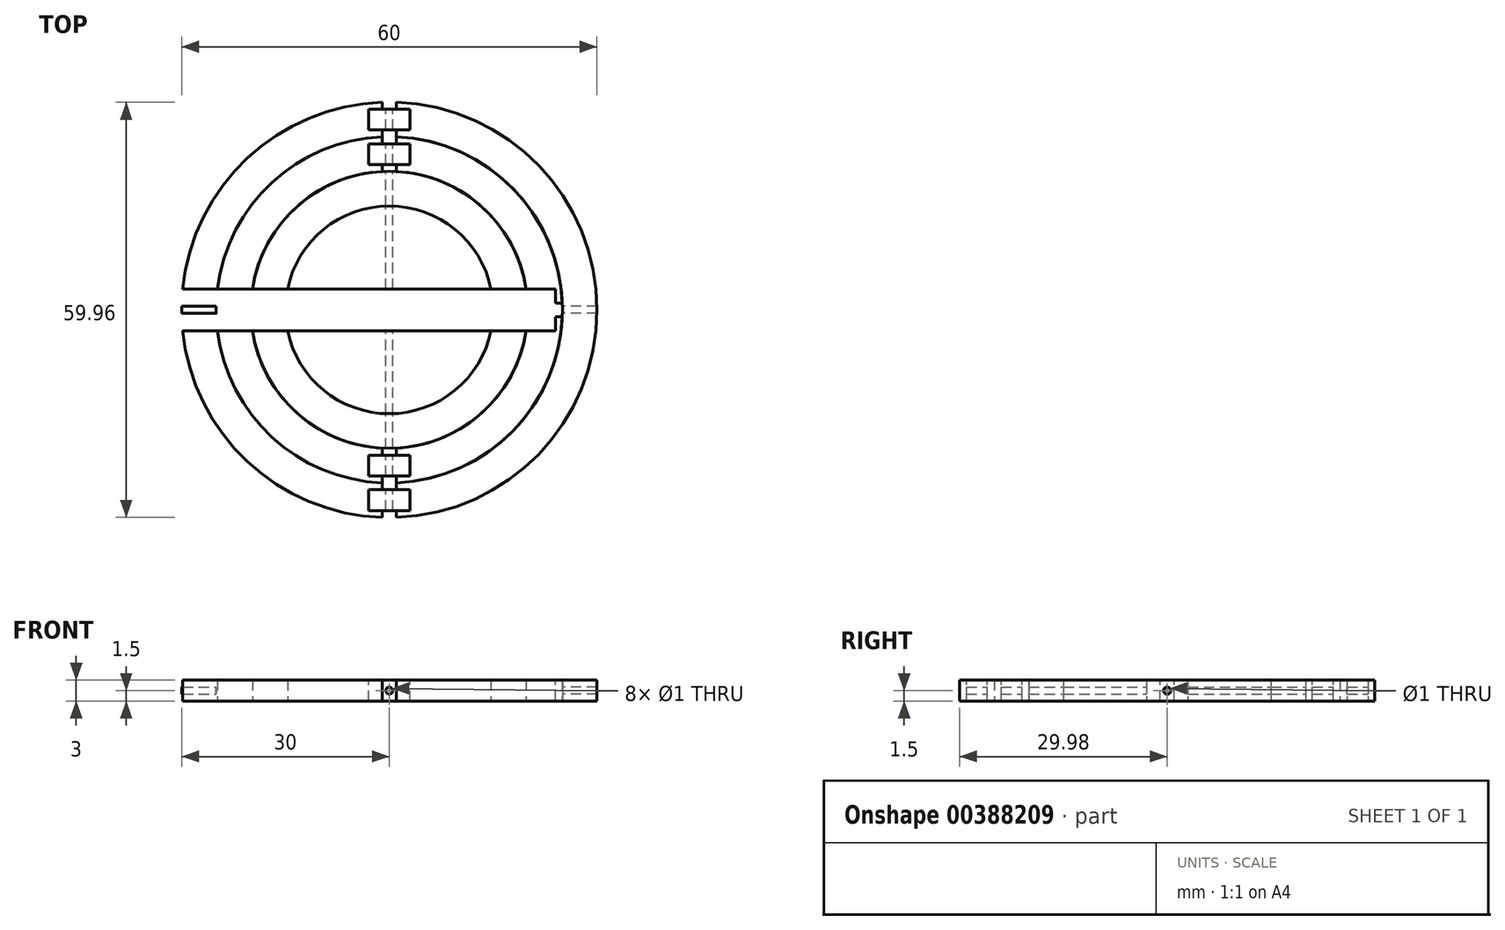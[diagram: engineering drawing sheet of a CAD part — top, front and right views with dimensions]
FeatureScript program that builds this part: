
annotation { "Feature Type Name" : "Feature", "Feature Type Description" : "" }
export const myFeature = defineFeature(function(context is Context, id is Id, definition is map)
    precondition{}
    {
        {
            assignVariable(context, id + "F0", {"name" : "WT", "anyValue" : 3});
        }
        {
            var Q0;
            Q0=qCreatedBy(makeId("Top.planeOp"),FACE);
            var sketch = newSketch(context, id + "F1", { "sketchPlane" : qUnion([Q0])});
            skCircle(sketch, "E0", {"center": v(0, 0) * mm, "radius": 30 * mm});
            skCircle(sketch, "E1", {"center": v(0, 0) * mm, "radius": 25 * mm});
            skCircle(sketch, "E2", {"center": v(0, 0) * mm, "radius": 20 * mm});
            skCircle(sketch, "E3", {"center": v(0, 0) * mm, "radius": 15 * mm});
            skLineSegment(sketch, "E4", {"start": v(-1, 29.98) * mm, "end": v(-1, 19.97) * mm});
            skLineSegment(sketch, "E5.MirrorCS", {"start": v(1, 29.98) * mm, "end": v(1, 19.97) * mm});
            skLineSegment(sketch, "E6.MirrorCS", {"start": v(-1, -29.98) * mm, "end": v(-1, -19.97) * mm});
            skLineSegment(sketch, "E7.MirrorCS", {"start": v(1, -29.98) * mm, "end": v(1, -19.97) * mm});
            skLineSegment(sketch, "E8", {"start": v(-14.97, 1) * mm, "end": v(-24.98, 1) * mm});
            skLineSegment(sketch, "E9.MirrorCS", {"start": v(-14.97, -1) * mm, "end": v(-24.98, -1) * mm});
            skLineSegment(sketch, "E10.MirrorCS", {"start": v(14.97, 1) * mm, "end": v(24.98, 1) * mm});
            skLineSegment(sketch, "E11.MirrorCS", {"start": v(14.97, -1) * mm, "end": v(24.98, -1) * mm});
            skSolve(sketch);
        }
        {
            var Q0;
            {var subQ5=sQuery(id+"F1.wireOp",EDGE,"E4");var subQ7=sQuery(id+"F1.wireOp",EDGE,"E0");var subQ9=makeQuery(id+"F1.imprint","INTERSECT",VERTEX,{"derivedFrom":[subQ7,subQ5]});Q0=makeQuery(id+"F1.imprint","IMPRINT",FACE,{"disambiguationData":[TD([[makeQuery(id+"F1.imprint","IMPRINT",EDGE,{"disambiguationData":[TD([[subQ9,-1.0]])],"derivedFrom":subQ7}),1.0]])]});}
            var Q1;
            {var subQ5=sQuery(id+"F1.wireOp",EDGE,"E5.MirrorCS");var subQ7=sQuery(id+"F1.wireOp",EDGE,"E0");var subQ8=makeQuery(id+"F1.imprint","INTERSECT",VERTEX,{"derivedFrom":[subQ7,subQ5]});Q1=makeQuery(id+"F1.imprint","IMPRINT",FACE,{"disambiguationData":[TD([[makeQuery(id+"F1.imprint","IMPRINT",EDGE,{"disambiguationData":[TD([[subQ8,1.0]])],"derivedFrom":subQ7}),1.0]])]});}
            extrude(context, id + "F2", {"entities" : qUnion([Q0, Q1]), "depth" : 1.5 * mm, "hasSecondDirection" : true, "secondDirectionOppositeDirection" : true, "secondDirectionDepth" : 1.5 * mm});
        }
        {
            var Q0;
            {var subQ0=sQuery(id+"F1.wireOp",EDGE,"E8");var subQ1=sQuery(id+"F1.wireOp",EDGE,"E1");var subQ2=makeQuery(id+"F1.imprint","INTERSECT",VERTEX,{"derivedFrom":[subQ1,subQ0]});Q0=makeQuery(id+"F1.imprint","IMPRINT",FACE,{"disambiguationData":[TD([[makeQuery(id+"F1.imprint","IMPRINT",EDGE,{"disambiguationData":[TD([[subQ2,1.0]])],"derivedFrom":subQ1}),1.0]])]});}
            var Q1;
            {var subQ0=sQuery(id+"F1.wireOp",EDGE,"E9.MirrorCS");var subQ1=sQuery(id+"F1.wireOp",EDGE,"E1");var subQ2=makeQuery(id+"F1.imprint","INTERSECT",VERTEX,{"derivedFrom":[subQ1,subQ0]});Q1=makeQuery(id+"F1.imprint","IMPRINT",FACE,{"disambiguationData":[TD([[makeQuery(id+"F1.imprint","IMPRINT",EDGE,{"disambiguationData":[TD([[subQ2,-1.0]])],"derivedFrom":subQ1}),1.0]])]});}
            var Q2;
            {var subQ0=sQuery(id+"F1.wireOp",EDGE,"E11.MirrorCS");var subQ1=sQuery(id+"F1.wireOp",EDGE,"E1");var subQ2=makeQuery(id+"F1.imprint","INTERSECT",VERTEX,{"derivedFrom":[subQ1,subQ0]});Q2=makeQuery(id+"F1.imprint","IMPRINT",FACE,{"disambiguationData":[TD([[makeQuery(id+"F1.imprint","IMPRINT",EDGE,{"disambiguationData":[TD([[subQ2,1.0]])],"derivedFrom":subQ1}),1.0]])]});}
            var Q3;
            {var subQ0=sQuery(id+"F1.wireOp",EDGE,"E10.MirrorCS");var subQ1=sQuery(id+"F1.wireOp",EDGE,"E1");var subQ2=makeQuery(id+"F1.imprint","INTERSECT",VERTEX,{"derivedFrom":[subQ1,subQ0]});Q3=makeQuery(id+"F1.imprint","IMPRINT",FACE,{"disambiguationData":[TD([[makeQuery(id+"F1.imprint","IMPRINT",EDGE,{"disambiguationData":[TD([[subQ2,-1.0]])],"derivedFrom":subQ1}),1.0]])]});}
            extrude(context, id + "F3", {"entities" : qUnion([Q0, Q1, Q2, Q3]), "depth" : 1.5 * mm, "hasSecondDirection" : true, "secondDirectionOppositeDirection" : true, "secondDirectionDepth" : 1.5 * mm});
        }
        {
            var Q0;
            {var subQ5=sQuery(id+"F1.wireOp",EDGE,"E2");var subQ9=makeQuery(id+"F1.imprint","INTERSECT",VERTEX,{"derivedFrom":[subQ5,sQuery(id+"F1.wireOp",EDGE,"E5.MirrorCS")]});Q0=makeQuery(id+"F1.imprint","IMPRINT",FACE,{"disambiguationData":[TD([[makeQuery(id+"F1.imprint","IMPRINT",EDGE,{"disambiguationData":[TD([[subQ9,1.0]])],"derivedFrom":subQ5}),1.0]])]});}
            var Q1;
            {var subQ0=sQuery(id+"F1.wireOp",EDGE,"E2");var subQ8=makeQuery(id+"F1.imprint","INTERSECT",VERTEX,{"derivedFrom":[subQ0,sQuery(id+"F1.wireOp",EDGE,"E6.MirrorCS")]});Q1=makeQuery(id+"F1.imprint","IMPRINT",FACE,{"disambiguationData":[TD([[makeQuery(id+"F1.imprint","IMPRINT",EDGE,{"disambiguationData":[TD([[subQ8,1.0]])],"derivedFrom":subQ0}),1.0]])]});}
            extrude(context, id + "F4", {"entities" : qUnion([Q0, Q1]), "depth" : 1.5 * mm, "hasSecondDirection" : true, "secondDirectionOppositeDirection" : true, "secondDirectionDepth" : 1.5 * mm});
        }
        {
            var Q0;
            {var subQ0=sQuery(id+"F1.wireOp",EDGE,"E3");var subQ1=makeQuery(id+"F1.imprint","INTERSECT",VERTEX,{"derivedFrom":[subQ0,sQuery(id+"F1.wireOp",EDGE,"E8")]});Q0=makeQuery(id+"F1.imprint","IMPRINT",FACE,{"disambiguationData":[TD([[makeQuery(id+"F1.imprint","IMPRINT",EDGE,{"disambiguationData":[TD([[subQ1,1.0]])],"derivedFrom":subQ0}),1.0]])]});}
            extrude(context, id + "F5", {"entities" : qUnion([Q0]), "depth" : (getVariable(context, 'WT')) / 2 * mm, "hasSecondDirection" : true, "secondDirectionOppositeDirection" : true, "secondDirectionDepth" : (getVariable(context, 'WT')) / 2 * mm});
        }
        {
            var Q0;
            Q0=makeQuery(id+"F2.opExtrude","CAP_FACE",FACE,{"disambiguationData":[OSD([sQuery(id+"F1.wireOp",EDGE,"E0"),sQuery(id+"F1.wireOp",EDGE,"E1"),sQuery(id+"F1.wireOp",EDGE,"E4"),sQuery(id+"F1.wireOp",EDGE,"E6.MirrorCS")])],"isStart":false});
            var sketch = newSketch(context, id + "F6", { "sketchPlane" : qUnion([Q0])});
            skLineSegment(sketch, "E12.0", {"start": v(-1, 29.98) * mm, "end": v(-1, 24.98) * mm, "construction": true});
            skLineSegment(sketch, "E13", {"start": v(-1, 27.48) * mm, "end": v(1, 27.48) * mm, "construction": true});
            skLineSegment(sketch, "E14.0", {"start": v(1, 29.98) * mm, "end": v(1, 24.98) * mm, "construction": true});
            skLineSegment(sketch, "E15.bottom", {"start": v(-3, 28.98) * mm, "end": v(3, 28.98) * mm});
            skLineSegment(sketch, "E15.top", {"start": v(-3, 25.98) * mm, "end": v(3, 25.98) * mm});
            skLineSegment(sketch, "E15.left", {"start": v(-3, 28.98) * mm, "end": v(-3, 25.98) * mm});
            skLineSegment(sketch, "E15.right", {"start": v(3, 28.98) * mm, "end": v(3, 25.98) * mm});
            skPoint(sketch, "E15.middle", {"position": v(0, 27.48) * mm});
            skLineSegment(sketch, "E16.0", {"start": v(-1, 24.98) * mm, "end": v(-1, 19.97) * mm, "construction": true});
            skLineSegment(sketch, "E17.0", {"start": v(1, 24.98) * mm, "end": v(1, 19.97) * mm, "construction": true});
            skLineSegment(sketch, "E18", {"start": v(-1, 22.48) * mm, "end": v(1, 22.48) * mm, "construction": true});
            skLineSegment(sketch, "E19.bottom", {"start": v(-3, 23.98) * mm, "end": v(3, 23.98) * mm});
            skLineSegment(sketch, "E19.top", {"start": v(-3, 20.98) * mm, "end": v(3, 20.98) * mm});
            skLineSegment(sketch, "E19.left", {"start": v(-3, 23.98) * mm, "end": v(-3, 20.98) * mm});
            skLineSegment(sketch, "E19.right", {"start": v(3, 23.98) * mm, "end": v(3, 20.98) * mm});
            skPoint(sketch, "E19.middle", {"position": v(0, 22.48) * mm});
            skLineSegment(sketch, "E20.0", {"start": v(-19.97, 1) * mm, "end": v(-24.98, 1) * mm});
            skLineSegment(sketch, "E21.0", {"start": v(-19.97, -1) * mm, "end": v(-24.98, -1) * mm});
            skLineSegment(sketch, "E22.0", {"start": v(-14.97, 1) * mm, "end": v(-19.97, 1) * mm});
            skLineSegment(sketch, "E23.0", {"start": v(-14.97, -1) * mm, "end": v(-19.97, -1) * mm});
            skLineSegment(sketch, "E24", {"start": v(-22.48, 1) * mm, "end": v(-22.48, -1) * mm, "construction": true});
            skLineSegment(sketch, "E25", {"start": v(-17.47, 1) * mm, "end": v(-17.47, -1) * mm, "construction": true});
            skLineSegment(sketch, "E26.bottom", {"start": v(-23.98, 3) * mm, "end": v(-20.98, 3) * mm});
            skLineSegment(sketch, "E26.top", {"start": v(-23.98, -3) * mm, "end": v(-20.98, -3) * mm});
            skLineSegment(sketch, "E26.left", {"start": v(-23.98, 3) * mm, "end": v(-23.98, -3) * mm});
            skLineSegment(sketch, "E26.right", {"start": v(-20.98, 3) * mm, "end": v(-20.98, -3) * mm});
            skPoint(sketch, "E26.middle", {"position": v(-22.48, 0) * mm});
            skLineSegment(sketch, "E27.bottom", {"start": v(-18.97, 3) * mm, "end": v(-15.97, 3) * mm});
            skLineSegment(sketch, "E27.top", {"start": v(-18.97, -3) * mm, "end": v(-15.97, -3) * mm});
            skLineSegment(sketch, "E27.left", {"start": v(-18.97, 3) * mm, "end": v(-18.97, -3) * mm});
            skLineSegment(sketch, "E27.right", {"start": v(-15.97, 3) * mm, "end": v(-15.97, -3) * mm});
            skPoint(sketch, "E27.middle", {"position": v(-17.47, 0) * mm});
            skLineSegment(sketch, "E28.MirrorCS", {"start": v(23.98, 3) * mm, "end": v(20.98, 3) * mm});
            skLineSegment(sketch, "E29.MirrorCS", {"start": v(23.98, 3) * mm, "end": v(23.98, -3) * mm});
            skLineSegment(sketch, "E30.MirrorCS", {"start": v(23.98, -3) * mm, "end": v(20.98, -3) * mm});
            skLineSegment(sketch, "E31.MirrorCS", {"start": v(20.98, 3) * mm, "end": v(20.98, -3) * mm});
            skLineSegment(sketch, "E32.MirrorCS", {"start": v(18.97, 3) * mm, "end": v(18.97, -3) * mm});
            skLineSegment(sketch, "E33.MirrorCS", {"start": v(18.97, 3) * mm, "end": v(15.97, 3) * mm});
            skLineSegment(sketch, "E34.MirrorCS", {"start": v(18.97, -3) * mm, "end": v(15.97, -3) * mm});
            skLineSegment(sketch, "E35.MirrorCS", {"start": v(15.97, 3) * mm, "end": v(15.97, -3) * mm});
            skLineSegment(sketch, "E36.MirrorCS", {"start": v(-3, -23.98) * mm, "end": v(3, -23.98) * mm});
            skLineSegment(sketch, "E37.MirrorCS", {"start": v(-3, -20.98) * mm, "end": v(3, -20.98) * mm});
            skLineSegment(sketch, "E38.MirrorCS", {"start": v(-3, -25.98) * mm, "end": v(3, -25.98) * mm});
            skLineSegment(sketch, "E39.MirrorCS", {"start": v(-3, -28.98) * mm, "end": v(3, -28.98) * mm});
            skLineSegment(sketch, "E40.MirrorCS", {"start": v(3, -28.98) * mm, "end": v(3, -25.98) * mm});
            skLineSegment(sketch, "E41.MirrorCS", {"start": v(3, -23.98) * mm, "end": v(3, -20.98) * mm});
            skLineSegment(sketch, "E42.MirrorCS", {"start": v(-3, -23.98) * mm, "end": v(-3, -20.98) * mm});
            skLineSegment(sketch, "E43.MirrorCS", {"start": v(-3, -28.98) * mm, "end": v(-3, -25.98) * mm});
            skLineSegment(sketch, "E44", {"start": v(-14.97, 1) * mm, "end": v(-13.47, 1) * mm});
            skLineSegment(sketch, "E45", {"start": v(-13.47, 1) * mm, "end": v(-13.47, 3) * mm});
            skLineSegment(sketch, "E46", {"start": v(-13.47, 3) * mm, "end": v(-10.47, 3) * mm});
            skLineSegment(sketch, "E47", {"start": v(-10.47, 3) * mm, "end": v(-10.47, -3) * mm});
            skPoint(sketch, "E47.endSnap0", {"position": v(-17.47, -3) * mm});
            skLineSegment(sketch, "E48", {"start": v(-10.47, -3) * mm, "end": v(-13.47, -3) * mm});
            skLineSegment(sketch, "E49", {"start": v(-13.47, -3) * mm, "end": v(-13.47, -1) * mm});
            skLineSegment(sketch, "E50", {"start": v(-13.47, -1) * mm, "end": v(-14.97, -1) * mm});
            skLineSegment(sketch, "E51", {"start": v(-13.47, -1) * mm, "end": v(-13.47, 1) * mm});
            skLineSegment(sketch, "E52.MirrorCS", {"start": v(10.47, 3) * mm, "end": v(10.47, -3) * mm});
            skLineSegment(sketch, "E53.MirrorCS", {"start": v(13.47, 3) * mm, "end": v(10.47, 3) * mm});
            skLineSegment(sketch, "E54.MirrorCS", {"start": v(14.97, 1) * mm, "end": v(13.47, 1) * mm});
            skLineSegment(sketch, "E55.MirrorCS", {"start": v(13.47, -1) * mm, "end": v(13.47, 1) * mm});
            skLineSegment(sketch, "E56.MirrorCS", {"start": v(13.47, -1) * mm, "end": v(14.97, -1) * mm});
            skLineSegment(sketch, "E57.MirrorCS", {"start": v(13.47, -3) * mm, "end": v(13.47, -1) * mm});
            skLineSegment(sketch, "E58.MirrorCS", {"start": v(10.47, -3) * mm, "end": v(13.47, -3) * mm});
            skLineSegment(sketch, "E59.MirrorCS", {"start": v(13.47, 1) * mm, "end": v(13.47, 3) * mm});
            skLineSegment(sketch, "E60", {"start": v(14.97, -1) * mm, "end": v(15.97, -1) * mm});
            skLineSegment(sketch, "E61", {"start": v(14.97, 1) * mm, "end": v(15.97, 1) * mm});
            skSolve(sketch);
        }
        {
            var Q0;
            {var subQ0=sQuery(id+"F6.wireOp",EDGE,"E15.right");Q0=makeQuery(id+"F6.imprint","IMPRINT",FACE,{"disambiguationData":[TD([[makeQuery(id+"F6.imprint","IMPRINT",EDGE,{"derivedFrom":subQ0}),-1.0]])]});}
            var Q1;
            {var subQ0=sQuery(id+"F6.wireOp",EDGE,"E15.left");Q1=makeQuery(id+"F6.imprint","IMPRINT",FACE,{"disambiguationData":[TD([[makeQuery(id+"F6.imprint","IMPRINT",EDGE,{"derivedFrom":subQ0}),1.0]])]});}
            var Q2;
            {var subQ0=sQuery(id+"F6.wireOp",EDGE,"E40.MirrorCS");Q2=makeQuery(id+"F6.imprint","IMPRINT",FACE,{"disambiguationData":[TD([[makeQuery(id+"F6.imprint","IMPRINT",EDGE,{"derivedFrom":subQ0}),1.0]])]});}
            var Q3;
            {var subQ0=sQuery(id+"F6.wireOp",EDGE,"E43.MirrorCS");Q3=makeQuery(id+"F6.imprint","IMPRINT",FACE,{"disambiguationData":[TD([[makeQuery(id+"F6.imprint","IMPRINT",EDGE,{"derivedFrom":subQ0}),-1.0]])]});}
            var Q4;
            Q4=makeQuery(id+"F6.imprint","IMPRINT",FACE,{"disambiguationData":[TD([[makeQuery(id+"F6.imprint","IMPRINT",EDGE,{"derivedFrom":sQuery(id+"F6.wireOp",EDGE,"E36.MirrorCS")}),1.0]])]});
            var Q5;
            Q5=makeQuery(id+"F6.imprint","IMPRINT",FACE,{"disambiguationData":[TD([[makeQuery(id+"F6.imprint","IMPRINT",EDGE,{"derivedFrom":sQuery(id+"F6.wireOp",EDGE,"E19.bottom")}),-1.0]])]});
            var Q6;
            Q6=makeQuery(id+"F6.imprint","IMPRINT",FACE,{"disambiguationData":[TD([[makeQuery(id+"F6.imprint","IMPRINT",EDGE,{"derivedFrom":sQuery(id+"F6.wireOp",EDGE,"E32.MirrorCS")}),-1.0]])]});
            var Q7;
            Q7=makeQuery(id+"F6.imprint","IMPRINT",FACE,{"disambiguationData":[TD([[makeQuery(id+"F6.imprint","IMPRINT",EDGE,{"derivedFrom":sQuery(id+"F6.wireOp",EDGE,"E28.MirrorCS")}),1.0]])]});
            var Q8;
            {var subQ5=sQuery(id+"F6.wireOp",EDGE,"E26.top");Q8=makeQuery(id+"F6.imprint","IMPRINT",FACE,{"disambiguationData":[TD([[makeQuery(id+"F6.imprint","IMPRINT",EDGE,{"derivedFrom":subQ5}),1.0]])]});}
            var Q9;
            {var subQ0=sQuery(id+"F6.wireOp",EDGE,"E26.right");var subQ1=sQuery(id+"F6.wireOp",EDGE,"E20.0");var subQ2=makeQuery(id+"F6.imprint","INTERSECT",VERTEX,{"derivedFrom":[subQ1,subQ0]});Q9=makeQuery(id+"F6.imprint","IMPRINT",FACE,{"disambiguationData":[TD([[makeQuery(id+"F6.imprint","IMPRINT",EDGE,{"disambiguationData":[TD([[subQ2,-1.0]])],"derivedFrom":subQ1}),1.0]])]});}
            var Q10;
            {var subQ5=sQuery(id+"F6.wireOp",EDGE,"E26.bottom");Q10=makeQuery(id+"F6.imprint","IMPRINT",FACE,{"disambiguationData":[TD([[makeQuery(id+"F6.imprint","IMPRINT",EDGE,{"derivedFrom":subQ5}),-1.0]])]});}
            var Q11;
            {var subQ5=sQuery(id+"F6.wireOp",EDGE,"E27.bottom");Q11=makeQuery(id+"F6.imprint","IMPRINT",FACE,{"disambiguationData":[TD([[makeQuery(id+"F6.imprint","IMPRINT",EDGE,{"derivedFrom":subQ5}),-1.0]])]});}
            var Q12;
            {var subQ0=sQuery(id+"F6.wireOp",EDGE,"E27.right");var subQ1=sQuery(id+"F6.wireOp",EDGE,"E22.0");var subQ2=makeQuery(id+"F6.imprint","INTERSECT",VERTEX,{"derivedFrom":[subQ1,subQ0]});Q12=makeQuery(id+"F6.imprint","IMPRINT",FACE,{"disambiguationData":[TD([[makeQuery(id+"F6.imprint","IMPRINT",EDGE,{"disambiguationData":[TD([[subQ2,-1.0]])],"derivedFrom":subQ1}),1.0]])]});}
            var Q13;
            {var subQ5=sQuery(id+"F6.wireOp",EDGE,"E27.top");Q13=makeQuery(id+"F6.imprint","IMPRINT",FACE,{"disambiguationData":[TD([[makeQuery(id+"F6.imprint","IMPRINT",EDGE,{"derivedFrom":subQ5}),1.0]])]});}
            var Q14;
            {var subQ4=sQuery(id+"F6.wireOp",EDGE,"E44");Q14=makeQuery(id+"F6.imprint","IMPRINT",FACE,{"disambiguationData":[TD([[makeQuery(id+"F6.imprint","IMPRINT",EDGE,{"derivedFrom":subQ4}),-1.0]])]});}
            var Q15;
            Q15=makeQuery(id+"F6.imprint","IMPRINT",FACE,{"disambiguationData":[TD([[makeQuery(id+"F6.imprint","IMPRINT",EDGE,{"derivedFrom":sQuery(id+"F6.wireOp",EDGE,"E45")}),-1.0]])]});
            var Q16;
            Q16=makeQuery(id+"F6.imprint","IMPRINT",FACE,{"disambiguationData":[TD([[makeQuery(id+"F6.imprint","IMPRINT",EDGE,{"derivedFrom":sQuery(id+"F6.wireOp",EDGE,"E52.MirrorCS")}),1.0]])]});
            var Q17;
            Q17=makeQuery(id+"F6.imprint","IMPRINT",FACE,{"disambiguationData":[TD([[makeQuery(id+"F6.imprint","IMPRINT",EDGE,{"derivedFrom":sQuery(id+"F6.wireOp",EDGE,"E54.MirrorCS")}),1.0]])]});
            extrude(context, id + "F7", {"entities" : qUnion([Q0, Q1, Q2, Q3, Q4, Q5, Q6, Q7, Q8, Q9, Q10, Q11, Q12, Q13, Q14, Q15, Q16, Q17]), "operationType" : NewBodyOperationType.REMOVE, "endBound" : BoundingType.THROUGH_ALL, "oppositeDirection" : true, "depth" : (getVariable(context, 'WT')) * mm});
        }
        {
            var Q0;
            {var subQ0=sQuery(id+"F6.wireOp",EDGE,"E15.left");Q0=makeQuery(id+"F6.imprint","IMPRINT",FACE,{"disambiguationData":[TD([[makeQuery(id+"F6.imprint","IMPRINT",EDGE,{"derivedFrom":subQ0}),1.0]])]});}
            var Q1;
            {var subQ0=sQuery(id+"F6.wireOp",EDGE,"E15.right");Q1=makeQuery(id+"F6.imprint","IMPRINT",FACE,{"disambiguationData":[TD([[makeQuery(id+"F6.imprint","IMPRINT",EDGE,{"derivedFrom":subQ0}),-1.0]])]});}
            var Q2;
            Q2=makeQuery(id+"F6.imprint","IMPRINT",FACE,{"disambiguationData":[TD([[makeQuery(id+"F6.imprint","IMPRINT",EDGE,{"derivedFrom":sQuery(id+"F6.wireOp",EDGE,"E19.bottom")}),-1.0]])]});
            var Q3;
            {var subQ0=sQuery(id+"F6.wireOp",EDGE,"E40.MirrorCS");Q3=makeQuery(id+"F6.imprint","IMPRINT",FACE,{"disambiguationData":[TD([[makeQuery(id+"F6.imprint","IMPRINT",EDGE,{"derivedFrom":subQ0}),1.0]])]});}
            var Q4;
            {var subQ0=sQuery(id+"F6.wireOp",EDGE,"E43.MirrorCS");Q4=makeQuery(id+"F6.imprint","IMPRINT",FACE,{"disambiguationData":[TD([[makeQuery(id+"F6.imprint","IMPRINT",EDGE,{"derivedFrom":subQ0}),-1.0]])]});}
            var Q5;
            Q5=makeQuery(id+"F6.imprint","IMPRINT",FACE,{"disambiguationData":[TD([[makeQuery(id+"F6.imprint","IMPRINT",EDGE,{"derivedFrom":sQuery(id+"F6.wireOp",EDGE,"E36.MirrorCS")}),1.0]])]});
            var Q6;
            {var subQ5=sQuery(id+"F6.wireOp",EDGE,"E26.bottom");Q6=makeQuery(id+"F6.imprint","IMPRINT",FACE,{"disambiguationData":[TD([[makeQuery(id+"F6.imprint","IMPRINT",EDGE,{"derivedFrom":subQ5}),-1.0]])]});}
            var Q7;
            {var subQ0=sQuery(id+"F6.wireOp",EDGE,"E26.right");var subQ1=sQuery(id+"F6.wireOp",EDGE,"E20.0");var subQ2=makeQuery(id+"F6.imprint","INTERSECT",VERTEX,{"derivedFrom":[subQ1,subQ0]});Q7=makeQuery(id+"F6.imprint","IMPRINT",FACE,{"disambiguationData":[TD([[makeQuery(id+"F6.imprint","IMPRINT",EDGE,{"disambiguationData":[TD([[subQ2,-1.0]])],"derivedFrom":subQ1}),1.0]])]});}
            var Q8;
            {var subQ5=sQuery(id+"F6.wireOp",EDGE,"E26.top");Q8=makeQuery(id+"F6.imprint","IMPRINT",FACE,{"disambiguationData":[TD([[makeQuery(id+"F6.imprint","IMPRINT",EDGE,{"derivedFrom":subQ5}),1.0]])]});}
            var Q9;
            {var subQ5=sQuery(id+"F6.wireOp",EDGE,"E27.bottom");Q9=makeQuery(id+"F6.imprint","IMPRINT",FACE,{"disambiguationData":[TD([[makeQuery(id+"F6.imprint","IMPRINT",EDGE,{"derivedFrom":subQ5}),-1.0]])]});}
            var Q10;
            {var subQ0=sQuery(id+"F6.wireOp",EDGE,"E27.right");var subQ1=sQuery(id+"F6.wireOp",EDGE,"E22.0");var subQ2=makeQuery(id+"F6.imprint","INTERSECT",VERTEX,{"derivedFrom":[subQ1,subQ0]});Q10=makeQuery(id+"F6.imprint","IMPRINT",FACE,{"disambiguationData":[TD([[makeQuery(id+"F6.imprint","IMPRINT",EDGE,{"disambiguationData":[TD([[subQ2,-1.0]])],"derivedFrom":subQ1}),1.0]])]});}
            var Q11;
            {var subQ5=sQuery(id+"F6.wireOp",EDGE,"E27.top");Q11=makeQuery(id+"F6.imprint","IMPRINT",FACE,{"disambiguationData":[TD([[makeQuery(id+"F6.imprint","IMPRINT",EDGE,{"derivedFrom":subQ5}),1.0]])]});}
            var Q12;
            Q12=makeQuery(id+"F6.imprint","IMPRINT",FACE,{"disambiguationData":[TD([[makeQuery(id+"F6.imprint","IMPRINT",EDGE,{"derivedFrom":sQuery(id+"F6.wireOp",EDGE,"E32.MirrorCS")}),-1.0]])]});
            var Q13;
            Q13=makeQuery(id+"F6.imprint","IMPRINT",FACE,{"disambiguationData":[TD([[makeQuery(id+"F6.imprint","IMPRINT",EDGE,{"derivedFrom":sQuery(id+"F6.wireOp",EDGE,"E28.MirrorCS")}),1.0]])]});
            var Q14;
            Q14=makeQuery(id+"F6.imprint","IMPRINT",FACE,{"disambiguationData":[TD([[makeQuery(id+"F6.imprint","IMPRINT",EDGE,{"derivedFrom":sQuery(id+"F6.wireOp",EDGE,"E45")}),-1.0]])]});
            var Q15;
            Q15=makeQuery(id+"F6.imprint","IMPRINT",FACE,{"disambiguationData":[TD([[makeQuery(id+"F6.imprint","IMPRINT",EDGE,{"derivedFrom":sQuery(id+"F6.wireOp",EDGE,"E52.MirrorCS")}),1.0]])]});
            extrude(context, id + "F8", {"entities" : qUnion([Q0, Q1, Q2, Q3, Q4, Q5, Q6, Q7, Q8, Q9, Q10, Q11, Q12, Q13, Q14, Q15]), "oppositeDirection" : true, "depth" : (getVariable(context, 'WT')) * mm});
        }
        {
            var Q0;
            Q0=makeQuery(id+"F8.opExtrude","SWEPT_FACE",FACE,{"disambiguationData":[OSD([sQuery(id+"F6.wireOp",EDGE,"E15.bottom")])]});
            var sketch = newSketch(context, id + "F9", { "sketchPlane" : qUnion([Q0])});
            skCircle(sketch, "E62", {"center": v(0, 0) * mm, "radius": 0.5 * mm});
            skSolve(sketch);
        }
        {
            var Q0;
            Q0=makeQuery(id+"F9.imprint","IMPRINT",FACE,{"disambiguationData":[TD([[makeQuery(id+"F9.imprint","IMPRINT",EDGE,{"derivedFrom":sQuery(id+"F9.wireOp",EDGE,"E62")}),1.0]])]});
            extrude(context, id + "F10", {"entities" : qUnion([Q0]), "operationType" : NewBodyOperationType.REMOVE, "endBound" : BoundingType.THROUGH_ALL, "oppositeDirection" : true, "depth" : 25 * mm});
        }
        {
            var Q0;
            Q0=makeQuery(id+"F8.opExtrude","SWEPT_FACE",FACE,{"disambiguationData":[OSD([sQuery(id+"F6.wireOp",EDGE,"E26.left")])]});
            var sketch = newSketch(context, id + "F11", { "sketchPlane" : qUnion([Q0])});
            skLineSegment(sketch, "E63.0", {"start": v(-3, -1.5) * mm, "end": v(3, -1.5) * mm});
            skLineSegment(sketch, "E64.0", {"start": v(-3, 1.5) * mm, "end": v(3, 1.5) * mm});
            skLineSegment(sketch, "E65", {"start": v(0, -1.5) * mm, "end": v(0, 1.5) * mm, "construction": true});
            skCircle(sketch, "E66", {"center": v(0, 0) * mm, "radius": 0.5 * mm});
            skSolve(sketch);
        }
        {
            var Q0;
            Q0=makeQuery(id+"F11.imprint","IMPRINT",FACE,{"disambiguationData":[TD([[makeQuery(id+"F11.imprint","IMPRINT",EDGE,{"derivedFrom":sQuery(id+"F11.wireOp",EDGE,"E66")}),1.0]])]});
            extrude(context, id + "F12", {"entities" : qUnion([Q0]), "operationType" : NewBodyOperationType.REMOVE, "endBound" : BoundingType.THROUGH_ALL, "oppositeDirection" : true, "depth" : 25 * mm});
        }
        {
            var Q0;
            Q0=makeQuery(id+"F8.opExtrude","SWEPT_FACE",FACE,{"disambiguationData":[OSD([sQuery(id+"F6.wireOp",EDGE,"E29.MirrorCS")])]});
            var sketch = newSketch(context, id + "F13", { "sketchPlane" : qUnion([Q0])});
            skCircle(sketch, "E67", {"center": v(0, 0) * mm, "radius": 0.5 * mm});
            skSolve(sketch);
        }
        {
            var Q0;
            Q0=makeQuery(id+"F13.imprint","IMPRINT",FACE,{"disambiguationData":[TD([[makeQuery(id+"F13.imprint","IMPRINT",EDGE,{"derivedFrom":sQuery(id+"F13.wireOp",EDGE,"E67")}),1.0]])]});
            extrude(context, id + "F14", {"entities" : qUnion([Q0]), "operationType" : NewBodyOperationType.REMOVE, "endBound" : BoundingType.THROUGH_ALL, "oppositeDirection" : true, "depth" : 25 * mm});
        }
        {
            var Q0;
            Q0=makeQuery(id+"F8.opExtrude","SWEPT_FACE",FACE,{"disambiguationData":[OSD([sQuery(id+"F6.wireOp",EDGE,"E39.MirrorCS")])]});
            var sketch = newSketch(context, id + "F15", { "sketchPlane" : qUnion([Q0])});
            skCircle(sketch, "E68", {"center": v(0, 0) * mm, "radius": 0.5 * mm});
            skSolve(sketch);
        }
        {
            var Q0;
            Q0=makeQuery(id+"F15.imprint","IMPRINT",FACE,{"disambiguationData":[TD([[makeQuery(id+"F15.imprint","IMPRINT",EDGE,{"derivedFrom":sQuery(id+"F15.wireOp",EDGE,"E68")}),1.0]])]});
            extrude(context, id + "F16", {"entities" : qUnion([Q0]), "operationType" : NewBodyOperationType.REMOVE, "endBound" : BoundingType.THROUGH_ALL, "oppositeDirection" : true, "depth" : 25 * mm});
        }
    });
